# Revit family: Q90.195.xxx.FU.WDAS_with 3 shelves_RV15
name_source: partatom
category: Möbelsysteme
revit_build: Autodesk Revit 2015 (Build: 20160512_1515(x64)
units: mm (PartAtom-declared; Revit-internal decimal feet)

## types (9) — shared parameters
1200 mm 4 drawers = Nein
1200 mm 6 drawers = Nein
600 mm 4 drawers = Nein
600 mm 6 drawers = Nein
900 mm 4 drawers = Nein
900 mm 6 drawers = Nein
Beschreibung = GS-tested safety storage cabinets for unrestricted storage of flammable hazardous materials in work areas in accordance with EN 14470-1 and TRGS 510 with a fire resistance of 90 (Type 90)
Cabinet colour = RAL 7016 Anthracite grey
Cabinet depth = 615 mm  [stored 2.01772 ft]
Cabinet height = 1954 mm
Diff. pressure (Air change 10 times) = 5.0 Pa
Hersteller = asecos GmbH
Price information = Price from summer 2018
Price information 2 = Prices are ex works and without taxes and shipping
Product video = https://www.youtube.com
URL = https://www.asecos.com

## per-type parameters (varying)
| type | 1200 mm 3 shelves | 600 mm 3 shelves | 900 mm 3 shelves | Air change 10 times | Air duct distance | Bestellnummer DACH | Cabinet width | Distributed load | Door colour | Door width | Double door | Handle position | Kosten | Modell | Order No. Global | Single door | Typenbild |
| Q90.195.060.FU.WDAS with 3 shelves, warning yellow | Nein | Ja | Nein | 1.1 L/s | 145 mm  [stored 0.475722 ft] | 37586-040-34765 | 600 mm | 8.77 kN/m² | RAL 1004 warning yellow | 512 mm  [stored 1.67979 ft] | Nein | 514 mm | 2258.5 $ | Q90.195.060.FU.WDAS with 3 shelves | 37586-040-34765 | Ja | 30072-040.jpg |
| Q90.195.060.FU.WDAS with 3 shelves, light grey | Nein | Ja | Nein | 1.1 L/s | 145 mm  [stored 0.475722 ft] | 37586-041-34765 | 600 mm | 8.77 kN/m² | RAL 7035 Light grey | 512 mm  [stored 1.67979 ft] | Nein | 514 mm | 2258.5 $ | Q90.195.060.FU.WDAS with 3 shelves | 37586-041-34765 | Ja | 30072-041.jpg |
| Q90.195.060.FU.WDAS with 3 shelves, pure white | Nein | Ja | Nein | 1.1 L/s | 145 mm  [stored 0.475722 ft] | 37586-050-34765 | 600 mm | 8.77 kN/m² | RAL 9010 Pure white | 512 mm  [stored 1.67979 ft] | Nein | 514 mm | 2258.5 $ | Q90.195.060.FU.WDAS with 3 shelves | 37586-050-34765 | Ja | 30072-050.jpg |
| Q90.195.090.FU.WDAS with 3 shelves, warning yellow | Nein | Nein | Ja | 1.7 L/s | 292 mm  [stored 0.958005 ft] | 37585-040-34761 | 894 mm | 6.41 kN/m² | RAL 1004 warning yellow | 399 mm | Ja | 401 mm | 2805 $ | Q90.195.090.FU.WDAS with 3 shelves | 37585-040-34761 | Nein | 30041-040.jpg |
| Q90.195.090.FU.WDAS with 3 shelves, light grey | Nein | Nein | Ja | 1.7 L/s | 292 mm  [stored 0.958005 ft] | 37585-041-34761 | 894 mm | 6.41 kN/m² | RAL 7035 Light grey | 399 mm | Ja | 401 mm | 2805 $ | Q90.195.090.FU.WDAS with 3 shelves | 37585-041-34761 | Nein | 30041-041.jpg |
| Q90.195.090.FU.WDAS with 3 shelves, pure white | Nein | Nein | Ja | 1.7 L/s | 292 mm  [stored 0.958005 ft] | 37585-050-34761 | 894 mm | 6.41 kN/m² | RAL 9010 Pure white | 399 mm | Ja | 401 mm | 2805 $ | Q90.195.090.FU.WDAS with 3 shelves | 37585-050-34761 | Nein | 30041-050.jpg |
| Q90.195.120.FU.WDAS with 3 shelves, warning yellow | Ja | Nein | Nein | 2.5 L/s | 442 mm  [stored 1.45013 ft] | 37584-040-34757 | 1194 mm | 4.16 kN/m² | RAL 1004 warning yellow | 549 mm | Ja | 551 mm | 2911 $ | Q90.195.120.FU.WDAS with 3 shelves | 37584-040-34757 | Nein | 30001-040.jpg |
| Q90.195.120.FU.WDAS with 3 shelves, light grey | Ja | Nein | Nein | 2.5 L/s | 442 mm  [stored 1.45013 ft] | 37584-041-34757 | 1194 mm | 4.16 kN/m² | RAL 7035 Light grey | 549 mm | Ja | 551 mm | 2911 $ | Q90.195.120.FU.WDAS with 3 shelves | 37584-041-34757 | Nein | 30001-041.jpg |
| Q90.195.120.FU.WDAS with 3 shelves, pure white | Ja | Nein | Nein | 2.5 L/s | 442 mm  [stored 1.45013 ft] | 37584-050-34757 | 1194 mm | 4.16 kN/m² | RAL 9010 Pure white | 549 mm | Ja | 551 mm | 2911 $ | Q90.195.120.FU.WDAS with 3 shelves | 37584-050-34757 | Nein | 30001-050.jpg |

note: [stored X ft] marks values corroborated as IEEE doubles in the binary element streams (Revit-internal decimal feet)
